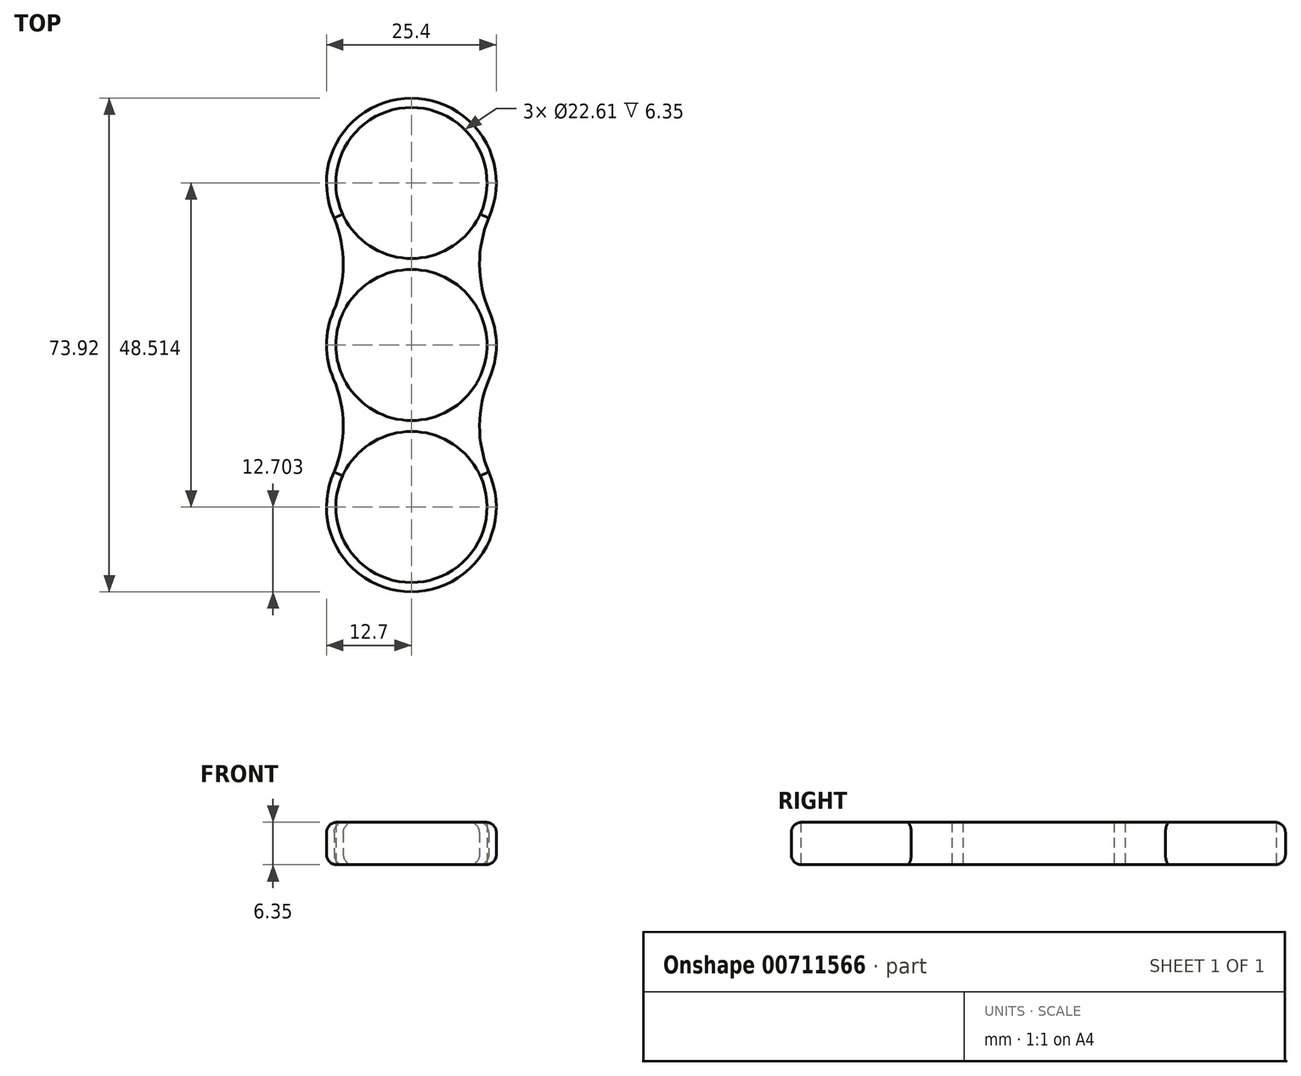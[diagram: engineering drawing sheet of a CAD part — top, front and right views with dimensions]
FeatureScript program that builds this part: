
annotation { "Feature Type Name" : "Feature", "Feature Type Description" : "" }
export const myFeature = defineFeature(function(context is Context, id is Id, definition is map)
    precondition{}
    {
        {
            var Q0;
            Q0=qCreatedBy(makeId("Top.planeOp"),FACE);
            var sketch = newSketch(context, id + "F0", { "sketchPlane" : qUnion([Q0])});
            skCircle(sketch, "E0", {"center": v(0, 0) * mm, "radius": 11.3 * mm});
            skCircle(sketch, "E1", {"center": v(0, 24.26) * mm, "radius": 11.3 * mm});
            skCircle(sketch, "E2.MirrorC", {"center": v(0, -24.26) * mm, "radius": 11.3 * mm});
            skPoint(sketch, "E3.MirrorCS.end.orphan", {"position": v(11.57, 21.83) * mm});
            skPoint(sketch, "E3.MirrorCS.start.orphan", {"position": v(11.67, 9.8) * mm});
            skPoint(sketch, "E4.MirrorCS.end.orphan", {"position": v(-11.57, 21.83) * mm});
            skPoint(sketch, "E4.MirrorCS.start.orphan", {"position": v(-11.67, 9.8) * mm});
            skPoint(sketch, "E5.MirrorCS.end.orphan", {"position": v(-11.57, -21.83) * mm});
            skPoint(sketch, "E5.MirrorCS.start.orphan", {"position": v(-11.67, -9.8) * mm});
            skPoint(sketch, "E6.end.orphan", {"position": v(11.57, -21.83) * mm});
            skPoint(sketch, "E6.start.orphan", {"position": v(11.67, -9.8) * mm});
            skArc(sketch, "E7", {"start": v(11.57, 19.02) * mm, "mid": v(0, 36.96) * mm, "end": v(-11.57, 19.02) * mm});
            skArc(sketch, "E8", {"start": v(-11.64, 5.08) * mm, "mid": v(-12.7, 0) * mm, "end": v(-11.64, -5.08) * mm});
            skArc(sketch, "E9", {"start": v(-11.57, -19.02) * mm, "mid": v(0, -36.96) * mm, "end": v(11.57, -19.02) * mm});
            skArc(sketch, "E10.trimOffspring", {"start": v(11.64, -5.08) * mm, "mid": v(12.7, 0) * mm, "end": v(11.64, 5.08) * mm});
            skArc(sketch, "E11", {"start": v(11.67, -5) * mm, "mid": v(10.2, -12) * mm, "end": v(11.57, -19.02) * mm});
            skArc(sketch, "E12.MirrorCS", {"start": v(-11.67, -5) * mm, "mid": v(-10.2, -12) * mm, "end": v(-11.57, -19.02) * mm});
            skArc(sketch, "E13.MirrorCS", {"start": v(11.67, 5) * mm, "mid": v(10.2, 12) * mm, "end": v(11.57, 19.02) * mm});
            skArc(sketch, "E14.MirrorCS", {"start": v(-11.67, 5) * mm, "mid": v(-10.2, 12) * mm, "end": v(-11.57, 19.02) * mm});
            skSolve(sketch);
        }
        {
            var Q0;
            Q0=qSketchRegion(id+"F0",true);
            extrude(context, id + "F1", {"entities" : qUnion([Q0]), "depth" : 6.35 * mm, "offsetDistance" : 25.4 * mm});
        }
        {
            var Q0;
            Q0=makeQuery(id+"F1.opExtrude","CAP_EDGE",EDGE,{"disambiguationData":[OSD([sQuery(id+"F0.wireOp",EDGE,"E8")])],"isStart":false});
            var Q1;
            Q1=makeQuery(id+"F1.opExtrude","CAP_EDGE",EDGE,{"disambiguationData":[OSD([sQuery(id+"F0.wireOp",EDGE,"E14.MirrorCS")])],"isStart":false});
            var Q2;
            Q2=makeQuery(id+"F1.opExtrude","CAP_EDGE",EDGE,{"disambiguationData":[OSD([sQuery(id+"F0.wireOp",EDGE,"E7")])],"isStart":false});
            var Q3;
            Q3=makeQuery(id+"F1.opExtrude","CAP_EDGE",EDGE,{"disambiguationData":[OSD([sQuery(id+"F0.wireOp",EDGE,"E13.MirrorCS")])],"isStart":false});
            var Q4;
            Q4=makeQuery(id+"F1.opExtrude","CAP_EDGE",EDGE,{"disambiguationData":[OSD([sQuery(id+"F0.wireOp",EDGE,"E10.trimOffspring")])],"isStart":false});
            var Q5;
            Q5=makeQuery(id+"F1.opExtrude","CAP_EDGE",EDGE,{"disambiguationData":[OSD([sQuery(id+"F0.wireOp",EDGE,"E11")])],"isStart":false});
            var Q6;
            Q6=makeQuery(id+"F1.opExtrude","CAP_EDGE",EDGE,{"disambiguationData":[OSD([sQuery(id+"F0.wireOp",EDGE,"E9")])],"isStart":false});
            var Q7;
            Q7=makeQuery(id+"F1.opExtrude","CAP_EDGE",EDGE,{"disambiguationData":[OSD([sQuery(id+"F0.wireOp",EDGE,"E12.MirrorCS")])],"isStart":false});
            var Q8;
            Q8=makeQuery(id+"F1.opExtrude","CAP_EDGE",EDGE,{"disambiguationData":[OSD([sQuery(id+"F0.wireOp",EDGE,"E7")])],"isStart":true});
            var Q9;
            Q9=makeQuery(id+"F1.opExtrude","CAP_EDGE",EDGE,{"disambiguationData":[OSD([sQuery(id+"F0.wireOp",EDGE,"E14.MirrorCS")])],"isStart":true});
            var Q10;
            Q10=makeQuery(id+"F1.opExtrude","CAP_EDGE",EDGE,{"disambiguationData":[OSD([sQuery(id+"F0.wireOp",EDGE,"E8")])],"isStart":true});
            var Q11;
            Q11=makeQuery(id+"F1.opExtrude","CAP_EDGE",EDGE,{"disambiguationData":[OSD([sQuery(id+"F0.wireOp",EDGE,"E12.MirrorCS")])],"isStart":true});
            var Q12;
            Q12=makeQuery(id+"F1.opExtrude","CAP_EDGE",EDGE,{"disambiguationData":[OSD([sQuery(id+"F0.wireOp",EDGE,"E9")])],"isStart":true});
            var Q13;
            Q13=makeQuery(id+"F1.opExtrude","CAP_EDGE",EDGE,{"disambiguationData":[OSD([sQuery(id+"F0.wireOp",EDGE,"E11")])],"isStart":true});
            var Q14;
            Q14=makeQuery(id+"F1.opExtrude","CAP_EDGE",EDGE,{"disambiguationData":[OSD([sQuery(id+"F0.wireOp",EDGE,"E10.trimOffspring")])],"isStart":true});
            var Q15;
            Q15=makeQuery(id+"F1.opExtrude","CAP_EDGE",EDGE,{"disambiguationData":[OSD([sQuery(id+"F0.wireOp",EDGE,"E13.MirrorCS")])],"isStart":true});
            fillet(context, id + "F2", {"entities" : qUnion([Q0, Q1, Q2, Q3, Q4, Q5, Q6, Q7, Q8, Q9, Q10, Q11, Q12, Q13, Q14, Q15]), "radius" : 1.52 * mm, "tangentPropagation" : true, "allowEdgeOverflow" : false});
        }
    });
